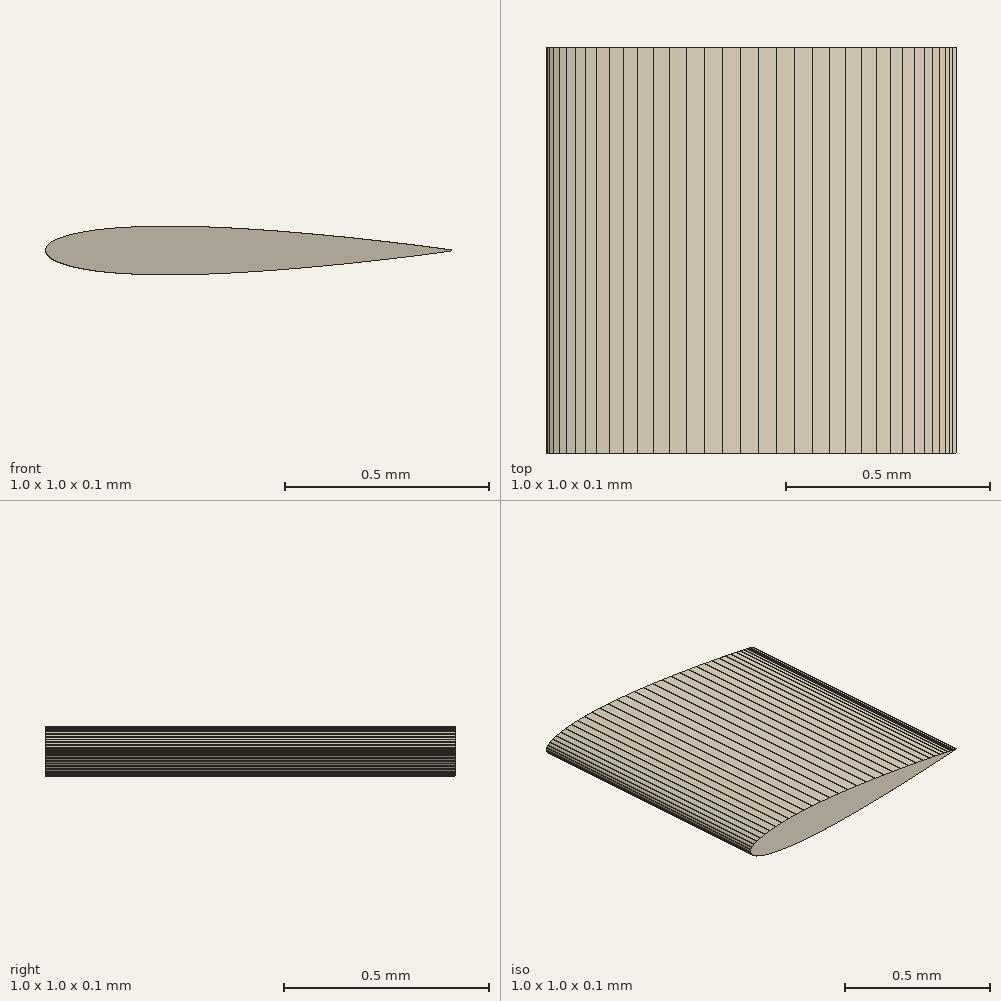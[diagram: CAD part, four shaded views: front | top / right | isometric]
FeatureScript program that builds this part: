
annotation { "Feature Type Name" : "Feature", "Feature Type Description" : "" }
export const myFeature = defineFeature(function(context is Context, id is Id, definition is map)
    precondition{}
    {
        {
            var Q0;
            Q0=qCreatedBy(makeId("Front.planeOp"),FACE);
            var sketch = newSketch(context, id + "F0", { "sketchPlane" : qUnion([Q0])});
            skLineSegment(sketch, "E0", {"start": v(0.5, 0) * mm, "end": v(0.5, 0) * mm});
            skLineSegment(sketch, "E1", {"start": v(0.5, 0) * mm, "end": v(0.48, 0) * mm});
            skLineSegment(sketch, "E2", {"start": v(0.48, 0) * mm, "end": v(0.47, 0) * mm});
            skLineSegment(sketch, "E3", {"start": v(0.47, 0) * mm, "end": v(0.45, 0) * mm});
            skLineSegment(sketch, "E4", {"start": v(0.45, 0) * mm, "end": v(0.43, 0.01) * mm});
            skLineSegment(sketch, "E5", {"start": v(0.43, 0.01) * mm, "end": v(0.4, 0.01) * mm});
            skLineSegment(sketch, "E6", {"start": v(0.4, 0.01) * mm, "end": v(0.38, 0.02) * mm});
            skLineSegment(sketch, "E7", {"start": v(0.38, 0.02) * mm, "end": v(0.35, 0.02) * mm});
            skLineSegment(sketch, "E8", {"start": v(0.35, 0.02) * mm, "end": v(0.31, 0.02) * mm});
            skLineSegment(sketch, "E9", {"start": v(0.31, 0.02) * mm, "end": v(0.28, 0.03) * mm});
            skLineSegment(sketch, "E10", {"start": v(0.28, 0.03) * mm, "end": v(0.24, 0.03) * mm});
            skLineSegment(sketch, "E11", {"start": v(0.24, 0.03) * mm, "end": v(0.2, 0.04) * mm});
            skLineSegment(sketch, "E12", {"start": v(0.2, 0.04) * mm, "end": v(0.15, 0.04) * mm});
            skLineSegment(sketch, "E13", {"start": v(0.15, 0.04) * mm, "end": v(0.11, 0.04) * mm});
            skLineSegment(sketch, "E14", {"start": v(0.11, 0.04) * mm, "end": v(0.07, 0.05) * mm});
            skLineSegment(sketch, "E15", {"start": v(0.07, 0.05) * mm, "end": v(0.02, 0.05) * mm});
            skLineSegment(sketch, "E16", {"start": v(0.02, 0.05) * mm, "end": v(-0.02, 0.05) * mm});
            skLineSegment(sketch, "E17", {"start": v(-0.02, 0.05) * mm, "end": v(-0.07, 0.06) * mm});
            skLineSegment(sketch, "E18", {"start": v(-0.07, 0.06) * mm, "end": v(-0.11, 0.06) * mm});
            skLineSegment(sketch, "E19", {"start": v(-0.11, 0.06) * mm, "end": v(-0.15, 0.06) * mm});
            skLineSegment(sketch, "E20", {"start": v(-0.15, 0.06) * mm, "end": v(-0.2, 0.06) * mm});
            skLineSegment(sketch, "E21", {"start": v(-0.2, 0.06) * mm, "end": v(-0.24, 0.06) * mm});
            skLineSegment(sketch, "E22", {"start": v(-0.24, 0.06) * mm, "end": v(-0.28, 0.06) * mm});
            skLineSegment(sketch, "E23", {"start": v(-0.28, 0.06) * mm, "end": v(-0.31, 0.06) * mm});
            skLineSegment(sketch, "E24", {"start": v(-0.31, 0.06) * mm, "end": v(-0.35, 0.05) * mm});
            skLineSegment(sketch, "E25", {"start": v(-0.35, 0.05) * mm, "end": v(-0.38, 0.05) * mm});
            skLineSegment(sketch, "E26", {"start": v(-0.38, 0.05) * mm, "end": v(-0.4, 0.05) * mm});
            skLineSegment(sketch, "E27", {"start": v(-0.4, 0.05) * mm, "end": v(-0.43, 0.04) * mm});
            skLineSegment(sketch, "E28", {"start": v(-0.43, 0.04) * mm, "end": v(-0.45, 0.04) * mm});
            skLineSegment(sketch, "E29", {"start": v(-0.45, 0.04) * mm, "end": v(-0.47, 0.03) * mm});
            skLineSegment(sketch, "E30", {"start": v(-0.47, 0.03) * mm, "end": v(-0.48, 0.02) * mm});
            skLineSegment(sketch, "E31", {"start": v(-0.48, 0.02) * mm, "end": v(-0.5, 0.02) * mm});
            skLineSegment(sketch, "E32", {"start": v(-0.5, 0.02) * mm, "end": v(-0.5, 0) * mm});
            skLineSegment(sketch, "E33", {"start": v(-0.5, 0) * mm, "end": v(-0.5, 0) * mm});
            skLineSegment(sketch, "E34", {"start": v(-0.5, 0) * mm, "end": v(-0.5, -0.02) * mm});
            skLineSegment(sketch, "E35", {"start": v(-0.5, -0.02) * mm, "end": v(-0.48, -0.02) * mm});
            skLineSegment(sketch, "E36", {"start": v(-0.48, -0.02) * mm, "end": v(-0.47, -0.03) * mm});
            skLineSegment(sketch, "E37", {"start": v(-0.47, -0.03) * mm, "end": v(-0.45, -0.04) * mm});
            skLineSegment(sketch, "E38", {"start": v(-0.45, -0.04) * mm, "end": v(-0.43, -0.04) * mm});
            skLineSegment(sketch, "E39", {"start": v(-0.43, -0.04) * mm, "end": v(-0.4, -0.05) * mm});
            skLineSegment(sketch, "E40", {"start": v(-0.4, -0.05) * mm, "end": v(-0.38, -0.05) * mm});
            skLineSegment(sketch, "E41", {"start": v(-0.38, -0.05) * mm, "end": v(-0.35, -0.05) * mm});
            skLineSegment(sketch, "E42", {"start": v(-0.35, -0.05) * mm, "end": v(-0.31, -0.06) * mm});
            skLineSegment(sketch, "E43", {"start": v(-0.31, -0.06) * mm, "end": v(-0.28, -0.06) * mm});
            skLineSegment(sketch, "E44", {"start": v(-0.28, -0.06) * mm, "end": v(-0.24, -0.06) * mm});
            skLineSegment(sketch, "E45", {"start": v(-0.24, -0.06) * mm, "end": v(-0.2, -0.06) * mm});
            skLineSegment(sketch, "E46", {"start": v(-0.2, -0.06) * mm, "end": v(-0.15, -0.06) * mm});
            skLineSegment(sketch, "E47", {"start": v(-0.15, -0.06) * mm, "end": v(-0.11, -0.06) * mm});
            skLineSegment(sketch, "E48", {"start": v(-0.11, -0.06) * mm, "end": v(-0.07, -0.06) * mm});
            skLineSegment(sketch, "E49", {"start": v(-0.07, -0.06) * mm, "end": v(-0.02, -0.05) * mm});
            skLineSegment(sketch, "E50", {"start": v(-0.02, -0.05) * mm, "end": v(0.02, -0.05) * mm});
            skLineSegment(sketch, "E51", {"start": v(0.02, -0.05) * mm, "end": v(0.07, -0.05) * mm});
            skLineSegment(sketch, "E52", {"start": v(0.07, -0.05) * mm, "end": v(0.11, -0.04) * mm});
            skLineSegment(sketch, "E53", {"start": v(0.11, -0.04) * mm, "end": v(0.15, -0.04) * mm});
            skLineSegment(sketch, "E54", {"start": v(0.15, -0.04) * mm, "end": v(0.2, -0.04) * mm});
            skLineSegment(sketch, "E55", {"start": v(0.2, -0.04) * mm, "end": v(0.24, -0.03) * mm});
            skLineSegment(sketch, "E56", {"start": v(0.24, -0.03) * mm, "end": v(0.28, -0.03) * mm});
            skLineSegment(sketch, "E57", {"start": v(0.28, -0.03) * mm, "end": v(0.31, -0.02) * mm});
            skLineSegment(sketch, "E58", {"start": v(0.31, -0.02) * mm, "end": v(0.35, -0.02) * mm});
            skLineSegment(sketch, "E59", {"start": v(0.35, -0.02) * mm, "end": v(0.38, -0.02) * mm});
            skLineSegment(sketch, "E60", {"start": v(0.38, -0.02) * mm, "end": v(0.4, -0.01) * mm});
            skLineSegment(sketch, "E61", {"start": v(0.4, -0.01) * mm, "end": v(0.43, -0.01) * mm});
            skLineSegment(sketch, "E62", {"start": v(0.43, -0.01) * mm, "end": v(0.45, 0) * mm});
            skLineSegment(sketch, "E63", {"start": v(0.45, 0) * mm, "end": v(0.47, 0) * mm});
            skLineSegment(sketch, "E64", {"start": v(0.47, 0) * mm, "end": v(0.48, 0) * mm});
            skLineSegment(sketch, "E65", {"start": v(0.48, 0) * mm, "end": v(0.5, 0) * mm});
            skSolve(sketch);
        }
        {
            var Q0;
            Q0 = qSketchRegion(id + "F0", true);
            extrude(context, id + "F1", {"entities" : qUnion([Q0]), "depth" : 1 * mm, "offsetDistance" : 25 * mm});
        }
    });
